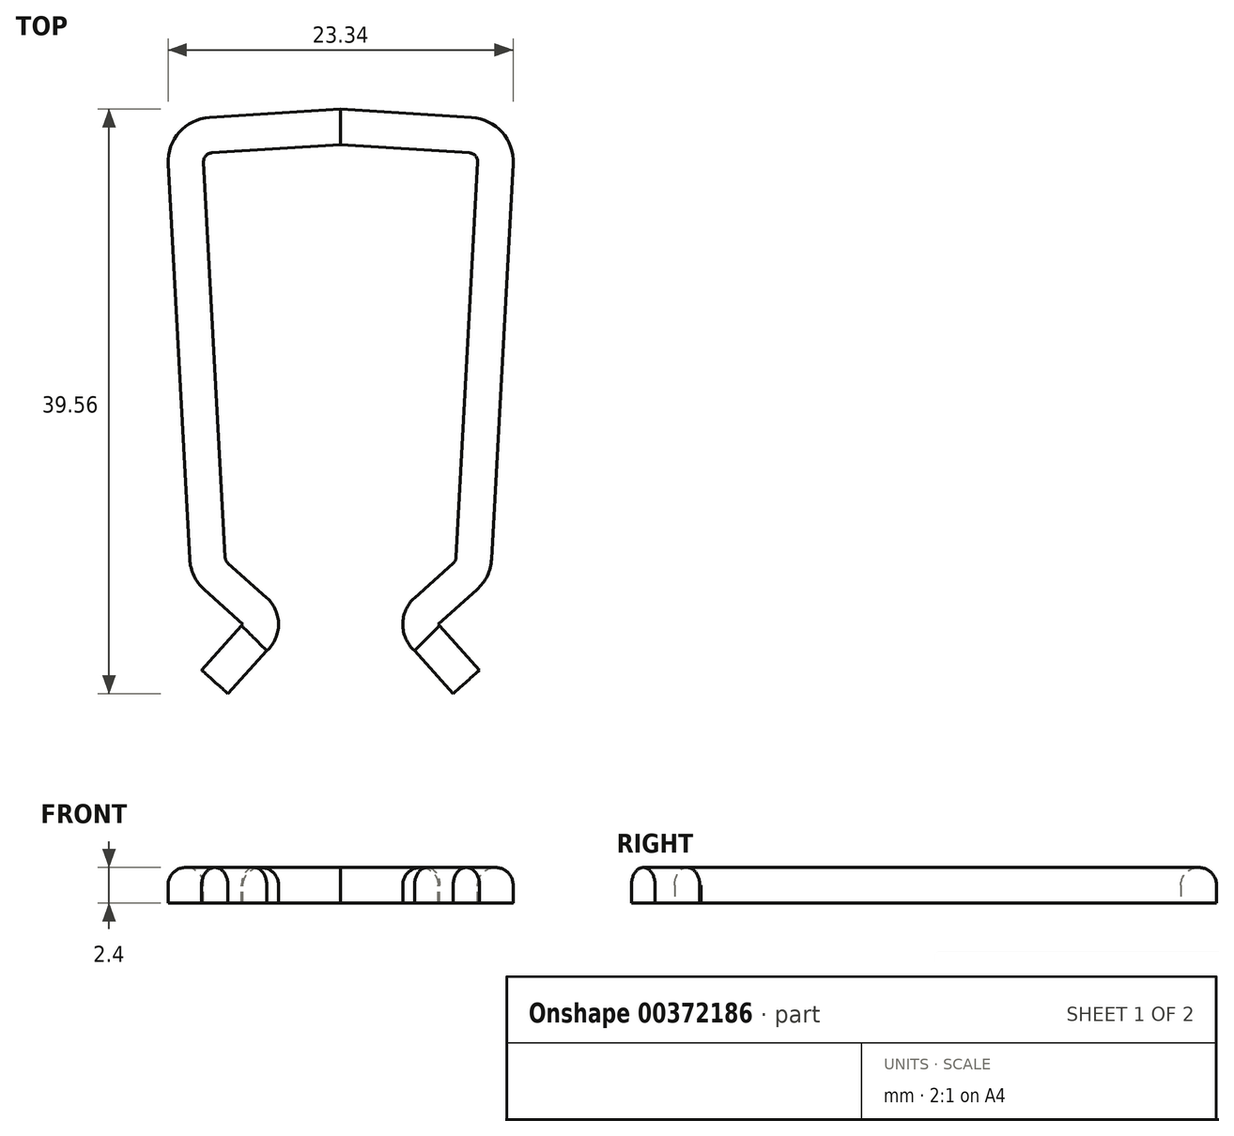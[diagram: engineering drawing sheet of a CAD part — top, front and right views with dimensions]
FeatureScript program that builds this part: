
annotation { "Feature Type Name" : "Feature", "Feature Type Description" : "" }
export const myFeature = defineFeature(function(context is Context, id is Id, definition is map)
    precondition{}
    {
        {
            var Q0;
            Q0=qCreatedBy(makeId("Top.planeOp"),FACE);
            var sketch = newSketch(context, id + "F0", { "sketchPlane" : qUnion([Q0])});
            skLineSegment(sketch, "E0", {"start": v(-2.6, -9.39) * mm, "end": v(2.6, -9.39) * mm, "construction": true});
            skPoint(sketch, "E1", {"position": v(0, -9.39) * mm});
            skLineSegment(sketch, "E2", {"start": v(2.6, -9.3) * mm, "end": v(3.09, -0.4) * mm});
            skLineSegment(sketch, "E3", {"start": v(2.9, -0.19) * mm, "end": v(0, 0) * mm});
            skLineSegment(sketch, "E4", {"start": v(0, 0) * mm, "end": v(-2.9, -0.19) * mm});
            skLineSegment(sketch, "E5", {"start": v(-3.09, -0.4) * mm, "end": v(-2.6, -9.3) * mm});
            skLineSegment(sketch, "E6", {"start": v(-3.1, -0.2) * mm, "end": v(3.1, -0.2) * mm, "construction": true});
            skPoint(sketch, "E7", {"position": v(0, -0.2) * mm});
            skLineSegment(sketch, "E8", {"start": v(2.54, -9.44) * mm, "end": v(1.67, -10.22) * mm});
            skArc(sketch, "E9", {"start": v(1.67, -10.22) * mm, "mid": v(1.4, -10.82) * mm, "end": v(1.67, -11.42) * mm});
            skLineSegment(sketch, "E10", {"start": v(1.67, -11.42) * mm, "end": v(2.54, -12.39) * mm});
            skLineSegment(sketch, "E11", {"start": v(0, -10.7) * mm, "end": v(2.2, -10.82) * mm, "construction": true});
            skLineSegment(sketch, "E12.MirrorCS", {"start": v(-1.67, -11.42) * mm, "end": v(-2.54, -12.39) * mm});
            skArc(sketch, "E13.MirrorCS", {"start": v(-1.67, -10.22) * mm, "mid": v(-1.4, -10.82) * mm, "end": v(-1.67, -11.42) * mm});
            skLineSegment(sketch, "E14.MirrorCS", {"start": v(0, -10.7) * mm, "end": v(-2.2, -10.82) * mm, "construction": true});
            skLineSegment(sketch, "E15.MirrorCS", {"start": v(-2.54, -9.44) * mm, "end": v(-1.67, -10.22) * mm});
            skPoint(sketch, "E16.visualSharp", {"position": v(2.6, -9.39) * mm});
            skArc(sketch, "E16.filletArc", {"start": v(2.54, -9.44) * mm, "mid": v(2.59, -9.38) * mm, "end": v(2.6, -9.3) * mm});
            skPoint(sketch, "E17.visualSharp", {"position": v(3.1, -0.2) * mm});
            skArc(sketch, "E17.filletArc", {"start": v(3.09, -0.4) * mm, "mid": v(3.04, -0.25) * mm, "end": v(2.9, -0.19) * mm});
            skPoint(sketch, "E18.visualSharp", {"position": v(-3.1, -0.2) * mm});
            skArc(sketch, "E18.filletArc", {"start": v(-2.9, -0.19) * mm, "mid": v(-3.04, -0.25) * mm, "end": v(-3.09, -0.4) * mm});
            skPoint(sketch, "E19.visualSharp", {"position": v(-2.6, -9.39) * mm});
            skArc(sketch, "E19.filletArc", {"start": v(-2.6, -9.3) * mm, "mid": v(-2.59, -9.38) * mm, "end": v(-2.54, -9.44) * mm});
            skSolve(sketch);
        }
        {
            var Q0;
            Q0=sQuery(id+"F0.wireOp",EDGE,"E10");
            var Q1;
            Q1=sQuery(id+"F0.wireOp",VERTEX,"E10.end");
            cPlane(context, id + "F1", {"entities" : qUnion([Q0, Q1]), "cplaneType" : CPlaneType.CURVE_POINT, "offset" : 12.18 * mm, "width" : 150 * mm, "height" : 150 * mm});
        }
        {
            var Q0;
            Q0=qCreatedBy(id+"F1.planeOp",FACE);
            var sketch = newSketch(context, id + "F2", { "sketchPlane" : qUnion([Q0])});
            skCircle(sketch, "E20", {"center": v(-5.98, 0) * mm, "radius": 0.4 * mm});
            skLineSegment(sketch, "E21", {"start": v(-6.38, 0) * mm, "end": v(-6.38, -0.4) * mm});
            skLineSegment(sketch, "E22", {"start": v(-6.38, -0.4) * mm, "end": v(-5.98, -0.4) * mm});
            skLineSegment(sketch, "E23", {"start": v(-5.98, -0.4) * mm, "end": v(-5.58, -0.4) * mm});
            skLineSegment(sketch, "E24", {"start": v(-5.58, -0.4) * mm, "end": v(-5.58, 0) * mm});
            skSolve(sketch);
        }
        {
            var Q0;
            Q0=makeQuery(id+"F2.imprint","IMPRINT",FACE,{"disambiguationData":[TD([[makeQuery(id+"F2.imprint","IMPRINT",EDGE,{"derivedFrom":sQuery(id+"F2.wireOp",EDGE,"E20")}),1.0]])]});
            var Q1;
            {var subQ0=sQuery(id+"F2.wireOp",EDGE,"E21");Q1=makeQuery(id+"F2.imprint","IMPRINT",FACE,{"disambiguationData":[TD([[makeQuery(id+"F2.imprint","IMPRINT",EDGE,{"derivedFrom":subQ0}),1.0]])]});}
            var Q2;
            {var subQ0=sQuery(id+"F2.wireOp",EDGE,"E23");Q2=makeQuery(id+"F2.imprint","IMPRINT",FACE,{"disambiguationData":[TD([[makeQuery(id+"F2.imprint","IMPRINT",EDGE,{"derivedFrom":subQ0}),1.0]])]});}
            var Q3;
            Q3=sQuery(id+"F0.wireOp",EDGE,"E10");
            var Q4;
            Q4=sQuery(id+"F0.wireOp",EDGE,"E9");
            var Q5;
            Q5=sQuery(id+"F0.wireOp",EDGE,"E8");
            var Q6;
            Q6=sQuery(id+"F0.wireOp",EDGE,"E16.filletArc");
            var Q7;
            Q7=sQuery(id+"F0.wireOp",EDGE,"E2");
            var Q8;
            Q8=sQuery(id+"F0.wireOp",EDGE,"E17.filletArc");
            var Q9;
            Q9=sQuery(id+"F0.wireOp",EDGE,"E3");
            var Q10;
            Q10=sQuery(id+"F0.wireOp",EDGE,"E4");
            var Q11;
            Q11=sQuery(id+"F0.wireOp",EDGE,"E18.filletArc");
            var Q12;
            Q12=sQuery(id+"F0.wireOp",EDGE,"E5");
            var Q13;
            Q13=sQuery(id+"F0.wireOp",EDGE,"E19.filletArc");
            var Q14;
            Q14=sQuery(id+"F0.wireOp",EDGE,"E15.MirrorCS");
            var Q15;
            Q15=sQuery(id+"F0.wireOp",EDGE,"E13.MirrorCS");
            var Q16;
            Q16=sQuery(id+"F0.wireOp",EDGE,"E12.MirrorCS");
            sweep(context, id + "F3", {"profiles" : qUnion([Q0, Q1, Q2]), "path" : qUnion([Q3, Q4, Q5, Q6, Q7, Q8, Q9, Q10, Q11, Q12, Q13, Q14, Q15, Q16])});
        }
        {
            var Q0;
            Q0=makeQuery(id+"F3.opSweep","SWEPT_BODY",BODY,{"disambiguationData":[OSD([sQuery(id+"F0.wireOp",EDGE,"E12.MirrorCS"),sQuery(id+"F2.wireOp",EDGE,"E20"),sQuery(id+"F2.wireOp",EDGE,"E21"),sQuery(id+"F2.wireOp",EDGE,"E22"),sQuery(id+"F2.wireOp",EDGE,"E23"),sQuery(id+"F2.wireOp",EDGE,"E24")])]});
            var Q1;
            Q1=qCreatedBy(makeId("Origin.pointOp"),VERTEX);
            transform(context, id + "F4", {"entities" : qUnion([Q0]), "transformType" : TransformType.SCALE_UNIFORMLY, "scale" : 3, "scalePoint" : qUnion([Q1]), "makeCopy" : false});
        }
    });
